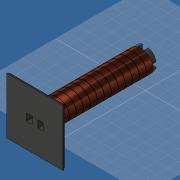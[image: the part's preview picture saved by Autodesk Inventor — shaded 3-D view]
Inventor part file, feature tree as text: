
AUTODESK INVENTOR PART (.ipt)
format: ipt  version: 2019 (Build 230136000, 136)  size: 435,200 bytes
history: native  units: mm
features: extrude x6, sketch x3, hole x1, other x1
ambient origin geometry x8: Origin, YZ Plane, XZ Plane, XY Plane, X Axis, Y Axis, Z Axis, Center Point
bodies: Volumenkörper1 (feature_tree)
feature tree (11):
  sketch  "Skizze1"  dims[d3=194.899mm d4=0.0mm d5=12.5mm]
  extrude  "Extrusion1"  Depth=12.5mm
  extrude  "Extrusion4"  Depth=9.5mm
  extrude  "Extrusion6"  Depth=10.0mm
  extrude  "Extrusion5"  Depth=10.0mm
  sketch  "Skizze2"  dims[d6=11.0mm d7=9.5mm]
  extrude  "Extrusion2"  Depth=10.0mm
  extrude  "Extrusion3"  Depth=10.0mm
  hole  "Bohrung1"  [1 undecoded]
  other  "Spirale1"
  sketch  "Skizze3"  dims[d9=1.0mm d10=1.0mm d12=9.0mm d14=40.0mm d15=13.5mm d16=30.5mm d17=30.0mm d18=9.5mm d19=100.0mm d20=100.0mm d21=1.2mm d22=2.0mm d23=0.0mm d24=2.0mm d25=0.0mm d26=12.0mm d27=0.5mm d28=12.5mm d29=180.0mm d30=160.0mm d31=0.0mm d32=90.0deg d33=90.0deg d34=0.0mm d35=0.0mm d37=40.0mm d40=2.2mm d41=4.0mm d42=4.0mm d43=2.0mm d44=90.0deg d45=5.0mm d46=0.0mm d47=30.0mm d48=90.0deg d49=45.0deg d50=10.5mm d52=10.0mm d53=0.0mm d55=8.0mm d56=6.0mm d57=0.0mm d58=17.0mm d59=0.0mm]
note: 1 required parameter value undecoded (feature->parameter linkage not recoverable at this tier; creation-order binding heuristic only, values carry confidence <= 0.55)
